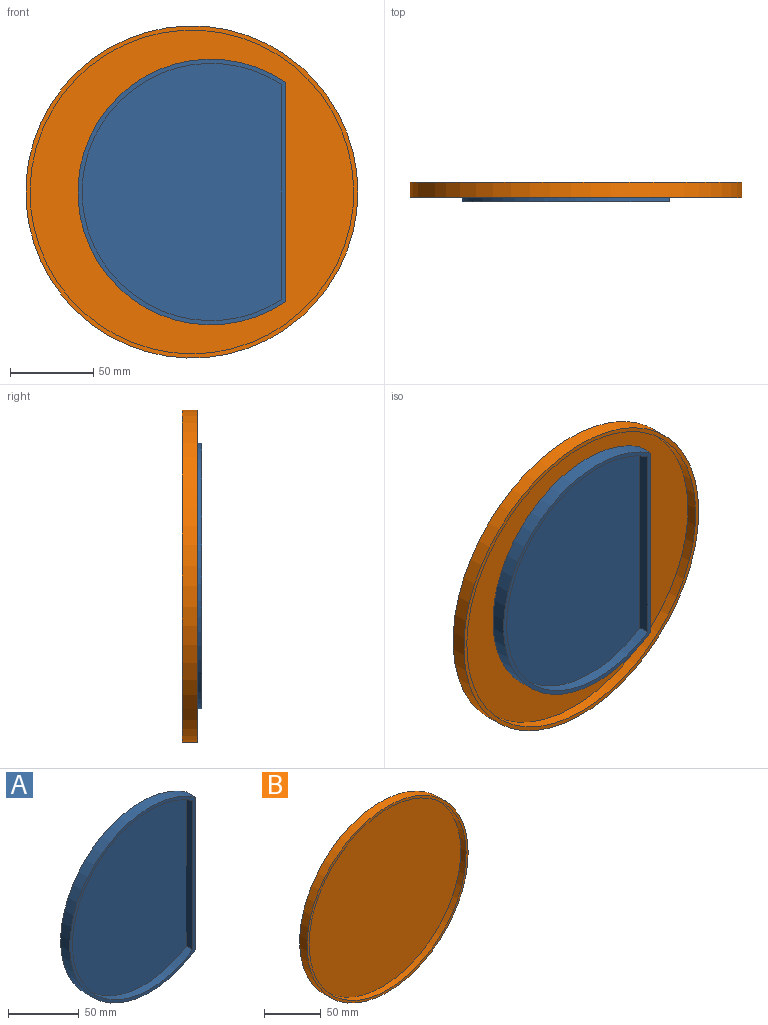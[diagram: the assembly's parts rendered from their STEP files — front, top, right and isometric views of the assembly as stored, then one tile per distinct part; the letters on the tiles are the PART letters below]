
ASSEMBLY  parts=2 mates=1
PART A: 7 faces, bbox 125.2x9.1x160 mm
  f0: plane 160x125.15mm, normal (0,-1,0), area 1196.8mm2, adj f1,f2,f4,f5
  f1: plane 132.08x9.14mm, normal (1,0,0), area 1207.7mm2, adj f0,f2,f3
  f2: cylinder r=80mm len=160mm, axis (0,1,0), area 3175.5mm2, adj f0,f1,f3
  f3: plane 160x125.15mm, normal (0,1,0), area 16873.1mm2, adj f1,f2
  f4: plane 129.37x6.6mm, normal (-1,0,0), area 854.4mm2, adj f0,f5,f6
  f5: cylinder r=77.46mm len=154.92mm, axis (0,1,0), area 2203mm2, adj f0,f4,f6
  f6: plane 154.92x120.07mm, normal (0,-1,0), area 15676.3mm2, adj f4,f5
PART B: 5 faces, bbox 200x9.1x200 mm
  f0: cylinder r=100mm len=200mm, axis (0,1,0), area 5745.3mm2, adj f1,f2
  f1: plane 200x200mm, normal (0,-1,0), area 1575.7mm2, adj f0,f3
  f2: plane 200x200mm, normal (0,1,0), area 31415.9mm2, adj f0
  f3: cylinder r=97.46mm len=194.92mm, axis (0,1,0), area 4044mm2, adj f1,f4
  f4: plane 194.92x194.92mm, normal (0,-1,0), area 29840.3mm2, adj f3
PLACE A rot(axis=(0,1,0),0deg) t=(204.98,121.45,-177.13)mm
PLACE B rot(axis=(0,1,0),0deg) t=(193.6,123.99,-177.13)mm
MATE fastened A.f3 <-> B.f0  axis (0,1,0) through (193.6,121.45,-177.13)mm
